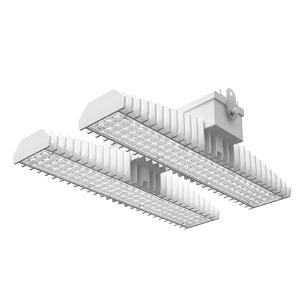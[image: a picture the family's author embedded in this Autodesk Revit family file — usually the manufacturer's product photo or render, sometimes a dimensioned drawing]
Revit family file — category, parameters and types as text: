
# Revit family: 3f_filippi_-_3f_lem_ho_ampio_3f_filippi_-_58954_a0811_-_3f_lem_2_ho_led_140_cr_ampio___vt_3550
name_source: partatom
category: Lighting Fixtures
units: mm (PartAtom-declared; Revit-internal decimal feet)

## family parameters
Cut with Voids When Loaded = No
Host = Face
Light Source = No
Part Type = Normal
Room Calculation Point = No
Round Connector Dimension = Use Diameter
Shared = No

## types (1)
- 3F Filippi - 3F LEM HO Ampio (1 x LED, 21051 lm, 138 W, 4000 K)
    Apparent Load = 138 VA
    Approval mark = CE
    CIE Flux Codes = 60 92 99 100 100
    Color Rendering = 80
    Color Temperature = 4000 K
    Control Gear = Electronic ballast
    Default Elevation = 1800 mm
    Description = Industrial luminaire with high light output and high luminous efficiency designed with the most innovative technologies for environments with temperature up to 55°C.

ILLUMINOTECHNICAL
Luminous efficiency 100% (DLOR 99%, ULOR 1%).
Initial luminous flux of the luminaire 21051 lm.
Direct symmetric wide distribution: the illuminated area has a rectangular shape.
Installation Interdistance Transv.D = 1.58 x hu - Long.D = 1.45 x hu.
Tabular UGR (CIE 117 - 4H-8H; S=0.25H; 70/50/20): RUG 23.1 - 24.2.
Beam angle: 93° - 99°.
Luminous efficacy 153 lm/W.
Lifetime (L93/B10): 30000 h. (tq+25°C)
Lifetime (L90/B10): 50000 h. (tq+25°C)
Lifetime (L85/B10): 80000 h. (tq+25°C)
Lifetime (L80/B10): 100000 h. (tq+25°C)
Lifetime (L85/B10): 50000 h. (tq+55°C)
Sudden decreased luminous flux after 50000 hours: 0% (C0).
Photobiological safety in compliance with IEC/TR 62778: RG0 risk exempt, (IEC 62471).
In compliance with IEC/EN 62722-2-1 - IEC/EN 62717 standards.

SOURCE
2 Mid-Power linear LED modules 70W/840.
Energy efficiency class (UE 2019/2020 - UE 2019/2015): C.
CIE 13.3 Colour rendering index: CRI >80 (R9 <50%).
IES TM-30 Fidelity Index: Rf = 84 Rg = 95.
CCT nominal colour temperature 4000 K.
Colour initial tolerance (MacAdam): SDCM 3.

MECHANICAL
Passive modular heatsinks in die-casted aluminium, painted in white colour.
To optimize the thermal management of the LED module, the heatsinks are oversized and provided with self-cleaning of cooling fins.
Wiring body in aluminium and galvanised steel anchored solidly to the sinks and thermally separated.
3F Lens lenses with high luminous efficiency, transparent methacrylate (PMMA), fixed to the LED modules.
Fixing brackets in stainless steel.
Luminaire with limited surface temperature. - D - (EN 60598-2-24)
Dimensions: 470x542 mm, height 133 mm. Weight 10.159 kg.
IP65 protection degree.
Mechanical strength to impacts IK06 (1 joule).
Glow-wire test resistance 650°C.

ELECTRICAL
Halogen Free electronic wiring 230V-50/60Hz, power factor 0.97, THD <25%, constant output current, class I, 1 driver.
Power of the luminaire 138 W.
ENEC - CE.
SAFE FLICKER: PstLM=<1 and SVM=<0.4 (IEC TR 61547-1 and IEC TR 63158), to ensure a more comfortable and safe light.
Luminaire compliant with EN 60598-2-22 for power supply from a centralised emergency system CPSS (Central Power Supply System), not incorporated in the luminaire - high risk areas excluded. The default power and flux are 100% in AC and 100% in DC.
Ambient temperature from -30°C to +55°C.
Temperature class T6 max 85°C.
Quick connection via M20 3P connector with 9-13 mm tightening range.
Power unit positioned on a separate compartment by the LED module to ensure optimum temperatures of cabling components, to be inspectable and maintainable.
Relative humidity UR: <85%.

INSTALLATION
Ceiling / Suspended / Wall.
All accessories dedicated to this product are available on the Catalog and on our website www.3F-Filippi.com.

ACCESSORIES
A0811 - VT transparent glass, tempered, not flammable, with sealing gasket.
One required for each light module. The pack contains 10 pieces.

APPLICATIONS
In commercial environments, exhibition and industrial areas, stores, open areas.
Environments in which it is necessary a total protection against falling fragments (eg environments with foodstuffs or machines with moving parts or with extreme temperature changes), use luminaires with polycarbonate lenses.

WARNING
Fixture not suitable for cold stores with an ambient temperature <0°C and/or relative humidity >85%.
Luminaire designed for disposal/recycling at end-of-life.
Replaceable (LED only) light source by a professional. Replaceable control gear by a professional.
    Height = 133 mm  [stored 0.436352 ft]
    Lamp = 1 x LED
    Lamp Light Flux = 21051 lm
    Lamp Power = 138 W
    Lamp count = 1
    Length = 470 mm
    Lifetime = 50000 h
    Luminous efficacy = 153 lm/W
    Manufacturer = 3F Filippi
    ModVariant = No
    Model = 3F Filippi - 58954+A0811 - 3F LEM 2 HO LED 140 CR AMPIO + VT
    Mounting Place = Ceiling
    Mounting Type = Pendant
    Number of Poles = 1
    OnlyDefault = Yes
    Power Factor = 1
    Product Name = 3F Filippi - 3F LEM HO Ampio
    Product group = pendant luminaire
    ProductGroupID = 9
    Protection Class = Protection class I
    Protection Degree = IP 65
    RLX_Detail_Level = 1
    RLX_Emergency_Light_Flux = 0 lm
    RLX_Emergency_Type = 0
    RLX_Emergency_Type_DB = No
    RlxData = <blob elided: 102517 chars, md5=2fffcc36>
    Socket = socket
    Standby Power = 0 W
    System Light Flux = 21051 lm
    System Power = 138 W
    Type Comments = Product without accessories
    Type Image = 3f_filippi_-_lem_2__a0811.jpg
    URL = http://relux.com
    VarID = ---
    Voltage = 0 V
    Weight = 0.00 kg
    Width = 542 mm

note: [stored X ft] marks values corroborated as IEEE doubles in the binary element streams (Revit-internal decimal feet)

## geometry (parser evidence)
native form markers: Blend x4, Sweep x14
no freeform markers — native parametric forms only
